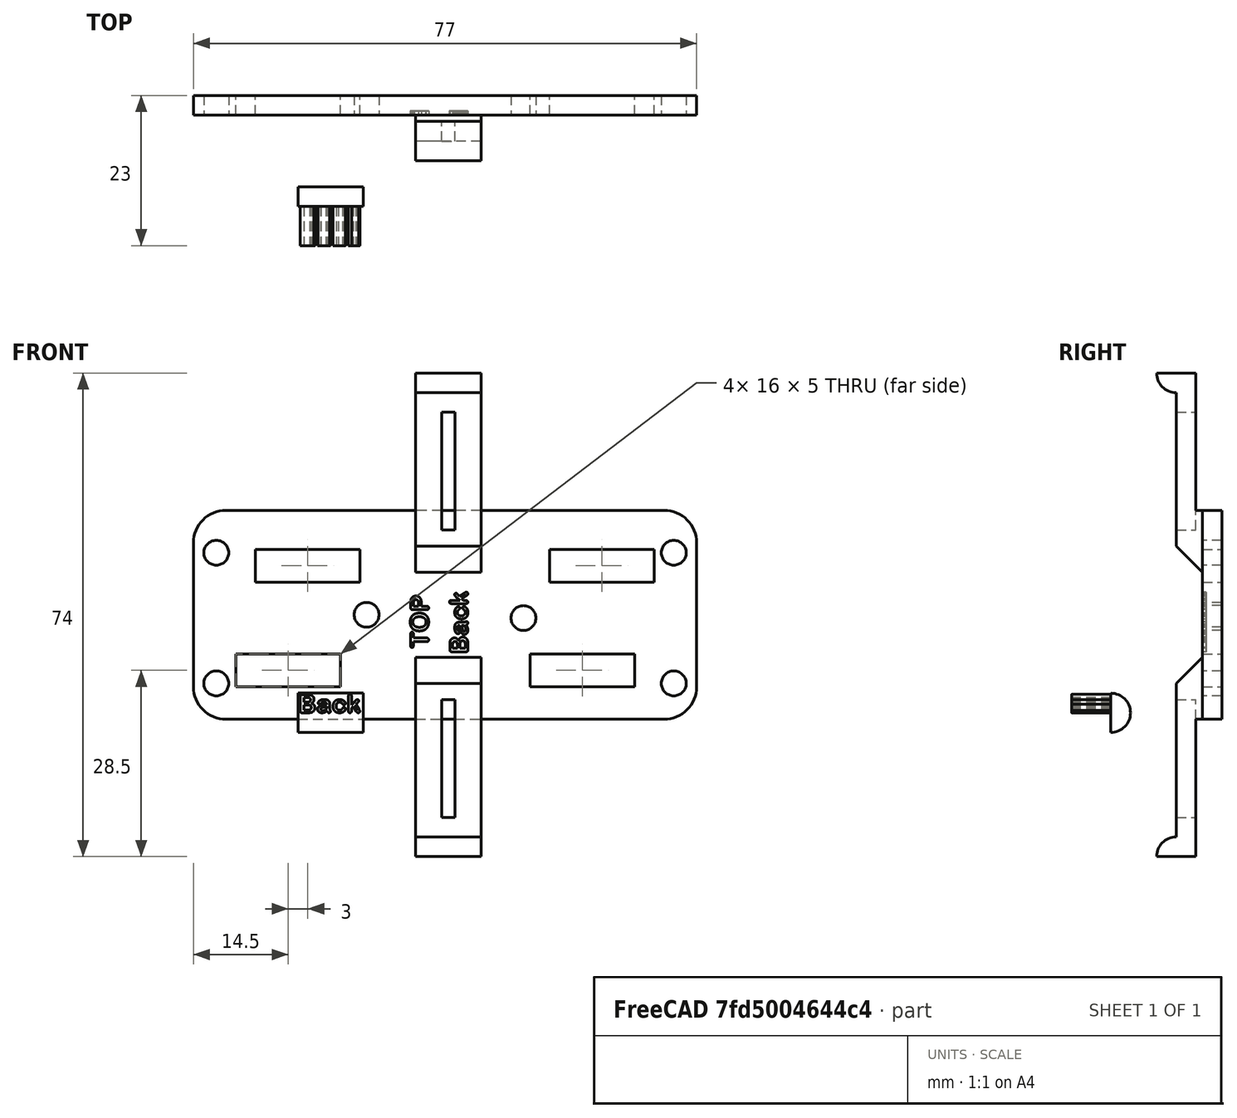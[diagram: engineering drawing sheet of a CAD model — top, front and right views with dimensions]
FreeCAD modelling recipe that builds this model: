
FCSTD DOCUMENT  (FreeCAD 0.16R6712 (Git))
Label: ParkingNozzleBasePlate
License: All rights reserved
LicenseURL: http://en.wikipedia.org/wiki/All_rights_reserved
objects: Part::Cylinder×15, Part::Box×13, Part::MultiFuse×11, Part::Cut×11, Part::Feature×6, Part::Part2DObjectPython×2, Part::Extrusion×1
note: 59 computed .brp shape members not serialized (recipe doc carries the construction recipe); baked Part::Feature solids carry a one-line shape summary decoded from their .brp

FEATURE [Part::Part2DObjectPython] ShapeString002  # Draft 2D object (typed FeaturePython)
  FontFile = <path>
  Size = 3
  String = TOP
  Tracking = 4
FEATURE [Part::Feature] Extrude001002001  label="Extrude001003"
  Placement = pos=(18,0,11) rot=(0,-1,0;1.5708rad)
  shape: bbox 2.835 x 6 x 7.877 mm, 76 faces, 3 solids (baked)
FEATURE [Part::Part2DObjectPython] ShapeString003  # Draft 2D object (typed FeaturePython)
  FontFile = <path>
  Size = 3
  String = Back
  Tracking = 4
FEATURE [Part::Extrusion] Extrude001002002
  Base = -> ShapeString003
  Dir = (0,0,6)
  Placement = pos=(0,0,0) rot=(1,0,0;1.5708rad)
  Solid = false
FEATURE [Part::Feature] Extrude001002002001  label="Extrude001002003"
  Placement = pos=(24,0,10) rot=(0,-1,0;1.5708rad)
  shape: bbox 2.835 x 6 x 9.142 mm, 140 faces, 4 solids (baked)
FEATURE [Part::Box] Box035  label="Würfel034"
  Height = 32
  Length = 77
  Placement = pos=(-16,14,-1) rot=(0,0,1;0rad)
  Width = 3
FEATURE [Part::MultiFuse] Fusion  label="Label"
  Placement = pos=(2,14.6,-1) rot=(0,0,1;0rad)
  Shapes = -> [Extrude001002002001,Extrude001002001]
FEATURE [Part::Cut] Cut
  Base = -> Box035
  Tool = -> Fusion
FEATURE [Part::Box] Box  label="Würfel"
  Height = 21
  Length = 10
  Placement = pos=(0,0,-2) rot=(0,0,1;0rad)
  Width = 3
FEATURE [Part::Cylinder] Cylinder  label="Zylinder"
  Angle = 180
  Height = 10
  Placement = pos=(0,0,0) rot=(0,1,0;1.5708rad)
  Radius = 3
FEATURE [Part::Feature] Cylinder040  label="Zylinder031"
  Placement = pos=(0,0,-2) rot=(1,0,0;1.5708rad)
  shape: bbox 10 x 6 x 3 mm, 4 faces (baked)
FEATURE [Part::MultiFuse] Fusion026006
  Placement = pos=(18,10,-20) rot=(0,0,1;0rad)
  Shapes = -> [Box,Cylinder040]
FEATURE [Part::Box] Box036  label="Würfel035"
  Height = 21
  Length = 10
  Placement = pos=(0,0,-2) rot=(0,0,1;0rad)
  Width = 3
FEATURE [Part::Feature] Cylinder041  label="Zylinder032"
  Placement = pos=(0,0,-2) rot=(1,0,0;1.5708rad)
  shape: bbox 10 x 6 x 3 mm, 4 faces (baked)
FEATURE [Part::MultiFuse] Fusion026007
  Placement = pos=(28,10,50) rot=(0,1,0;3.14159rad)
  Shapes = -> [Box036,Cylinder041]
FEATURE [Part::Cylinder] Cylinder051  label="Zylinder042"
  Angle = 90
  Height = 40
  Placement = pos=(33,25,29) rot=(1,0,0;1.5708rad)
  Radius = 8
FEATURE [Part::Cylinder] Cylinder052  label="Zylinder043"
  Angle = 90
  Height = 40
  Placement = pos=(33,25,29) rot=(1,0,0;1.5708rad)
  Radius = 5
FEATURE [Part::Cut] Cut011004004
  Base = -> Cylinder051
  Placement = pos=(18,0,-7) rot=(0,-1,0;1.5708rad)
  Tool = -> Cylinder052
FEATURE [Part::Cylinder] Cylinder053  label="Zylinder044"
  Angle = 90
  Height = 40
  Placement = pos=(33,25,29) rot=(1,0,0;1.5708rad)
  Radius = 8
FEATURE [Part::Cylinder] Cylinder054  label="Zylinder045"
  Angle = 90
  Height = 40
  Placement = pos=(33,25,29) rot=(1,0,0;1.5708rad)
  Radius = 5
FEATURE [Part::Cut] Cut011004005
  Base = -> Cylinder053
  Placement = pos=(22,0,33) rot=(0,1,0;3.14159rad)
  Tool = -> Cylinder054
FEATURE [Part::Cylinder] Cylinder055  label="Zylinder046"
  Angle = 90
  Height = 40
  Placement = pos=(33,25,29) rot=(1,0,0;1.5708rad)
  Radius = 8
FEATURE [Part::Cylinder] Cylinder056  label="Zylinder047"
  Angle = 90
  Height = 40
  Placement = pos=(33,25,29) rot=(1,0,0;1.5708rad)
  Radius = 5
FEATURE [Part::Cut] Cut011004006
  Base = -> Cylinder055
  Placement = pos=(23,0,-3) rot=(0,0,1;0rad)
  Tool = -> Cylinder056
FEATURE [Part::Cylinder] Cylinder059  label="Zylinder050"
  Angle = 90
  Height = 40
  Placement = pos=(33,25,29) rot=(1,0,0;1.5708rad)
  Radius = 8
FEATURE [Part::Cylinder] Cylinder060  label="Zylinder051"
  Angle = 90
  Height = 40
  Placement = pos=(33,25,29) rot=(1,0,0;1.5708rad)
  Radius = 5
FEATURE [Part::Cut] Cut011004008
  Base = -> Cylinder059
  Placement = pos=(27,0,37) rot=(0,1,0;1.5708rad)
  Tool = -> Cylinder060
FEATURE [Part::MultiFuse] Fusion026012  label="RoundEdges"
  Shapes = -> [Cut011004008,Cut011004006,Cut011004004,Cut011004005]
FEATURE [Part::Box] Box037  label="Würfel036"
  Height = 10
  Length = 10
  Width = 4
FEATURE [Part::Box] Box038  label="Würfel037"
  Height = 10
  Length = 10
  Placement = pos=(0,-5,9) rot=(-1,0,0;0.785398rad)
  Width = 6
FEATURE [Part::Cut] Cut011004009
  Base = -> Box037
  Placement = pos=(18,10,-1) rot=(0,0,1;0rad)
  Tool = -> Box038
FEATURE [Part::Box] Box039  label="Würfel038"
  Height = 10
  Length = 10
  Width = 4
FEATURE [Part::Box] Box040  label="Würfel039"
  Height = 10
  Length = 10
  Placement = pos=(0,-5,9) rot=(-1,0,0;0.785398rad)
  Width = 6
FEATURE [Part::Cut] Cut011004010
  Base = -> Box039
  Placement = pos=(28,10,31) rot=(0,1,0;3.14159rad)
  Tool = -> Box040
FEATURE [Part::Box] Box041  label="Würfel040"
  Height = 18
  Length = 2
  Placement = pos=(22,-1,-16) rot=(0,0,1;0rad)
  Width = 14
FEATURE [Part::Box] Box042  label="Würfel041"
  Height = 18
  Length = 2
  Placement = pos=(22,-1,28) rot=(0,0,1;0rad)
  Width = 14
FEATURE [Part::MultiFuse] Fusion026013
  Shapes = -> [Fusion026007,Cut011004010]
FEATURE [Part::Cut] Cut011004011  label="DecuplerLeft"
  Base = -> Fusion026013
  Tool = -> Box042
FEATURE [Part::MultiFuse] Fusion026014
  Shapes = -> [Fusion026006,Cut011004009]
FEATURE [Part::Cut] Cut011004012  label="DecuplerRight"
  Base = -> Fusion026014
  Tool = -> Box041
FEATURE [Part::Cylinder] Cylinder034  label="Zylinder025"
  Angle = 360
  Height = 26
  Placement = pos=(-13,16,4.5) rot=(1,0,0;1.5708rad)
  Radius = 1.9
FEATURE [Part::Cylinder] Cylinder035  label="Zylinder026"
  Angle = 360
  Height = 26
  Placement = pos=(-13,16,24.5) rot=(1,0,0;1.5708rad)
  Radius = 1.9
FEATURE [Part::Cylinder] Cylinder036  label="Zylinder027"
  Angle = 360
  Height = 26
  Placement = pos=(10.5,16,15) rot=(1,0,0;1.5708rad)
  Radius = 1.9
FEATURE [Part::MultiFuse] Fusion026003
  Placement = pos=(0.5,0,0) rot=(0,0,1;0rad)
  Shapes = -> [Cylinder034,Cylinder035]
FEATURE [Part::Cylinder] Cylinder037  label="Zylinder028"
  Angle = 360
  Height = 26
  Placement = pos=(-13,16,4.5) rot=(1,0,0;1.5708rad)
  Radius = 1.9
FEATURE [Part::Cylinder] Cylinder038  label="Zylinder029"
  Angle = 360
  Height = 26
  Placement = pos=(-13,16,24.5) rot=(1,0,0;1.5708rad)
  Radius = 1.9
FEATURE [Part::MultiFuse] Fusion026004
  Placement = pos=(70.5,0,0) rot=(0,0,1;0rad)
  Shapes = -> [Cylinder037,Cylinder038]
FEATURE [Part::Cylinder] Cylinder039  label="Zylinder030"
  Angle = 360
  Height = 26
  Placement = pos=(34.5,16,14.5) rot=(1,0,0;1.5708rad)
  Radius = 1.9
FEATURE [Part::MultiFuse] Fusion026005  label="Bohrung"
  Placement = pos=(0,3,0) rot=(0,0,1;0rad)
  Shapes = -> [Cylinder036,Fusion026003,Fusion026004,Cylinder039]
FEATURE [Part::MultiFuse] Fusion026015
  Shapes = -> [Fusion026012,Fusion026005]
FEATURE [Part::Cut] Cut011004013  label="BasePlate"
  Base = -> Cut
  Tool = -> Fusion026015
FEATURE [Part::Box] Box034  label="Würfel033"
  Height = 5
  Length = 16
  Placement = pos=(-9.5,-18,4) rot=(0,0,1;0rad)
  Width = 10
FEATURE [Part::Box] Box043  label="Würfel042"
  Height = 5
  Length = 16
  Placement = pos=(35.5,-18,4) rot=(0,0,1;0rad)
  Width = 10
FEATURE [Part::Box] Box044  label="Würfel043"
  Height = 5
  Length = 16
  Placement = pos=(-6.5,-18,20) rot=(0,0,1;0rad)
  Width = 10
FEATURE [Part::Box] Box045  label="Würfel044"
  Height = 5
  Length = 16
  Placement = pos=(38.5,-18,20) rot=(0,0,1;0rad)
  Width = 10
FEATURE [Part::MultiFuse] Fusion026017  label="SripperHoles"
  Placement = pos=(0,26,0) rot=(0,0,1;0rad)
  Shapes = -> [Box034,Box045,Box043,Box044]
FEATURE [Part::Cut] Cut011004014  label="BasePlateOpen"
  Base = -> Cut011004013
  Tool = -> Fusion026017
FEATURE [Part::Feature] Cut011004014001  label="BasePlateOpen_export"
  shape: bbox 77 x 3 x 32 mm, 246 faces (baked)
FEATURE [Part::Feature] Cut011004013001  label="BasePlate_export"
  shape: bbox 77 x 3 x 32 mm, 230 faces (baked)
note: 2 file-system paths scrubbed to <path> (originals preserved in the JSON sidecar)
